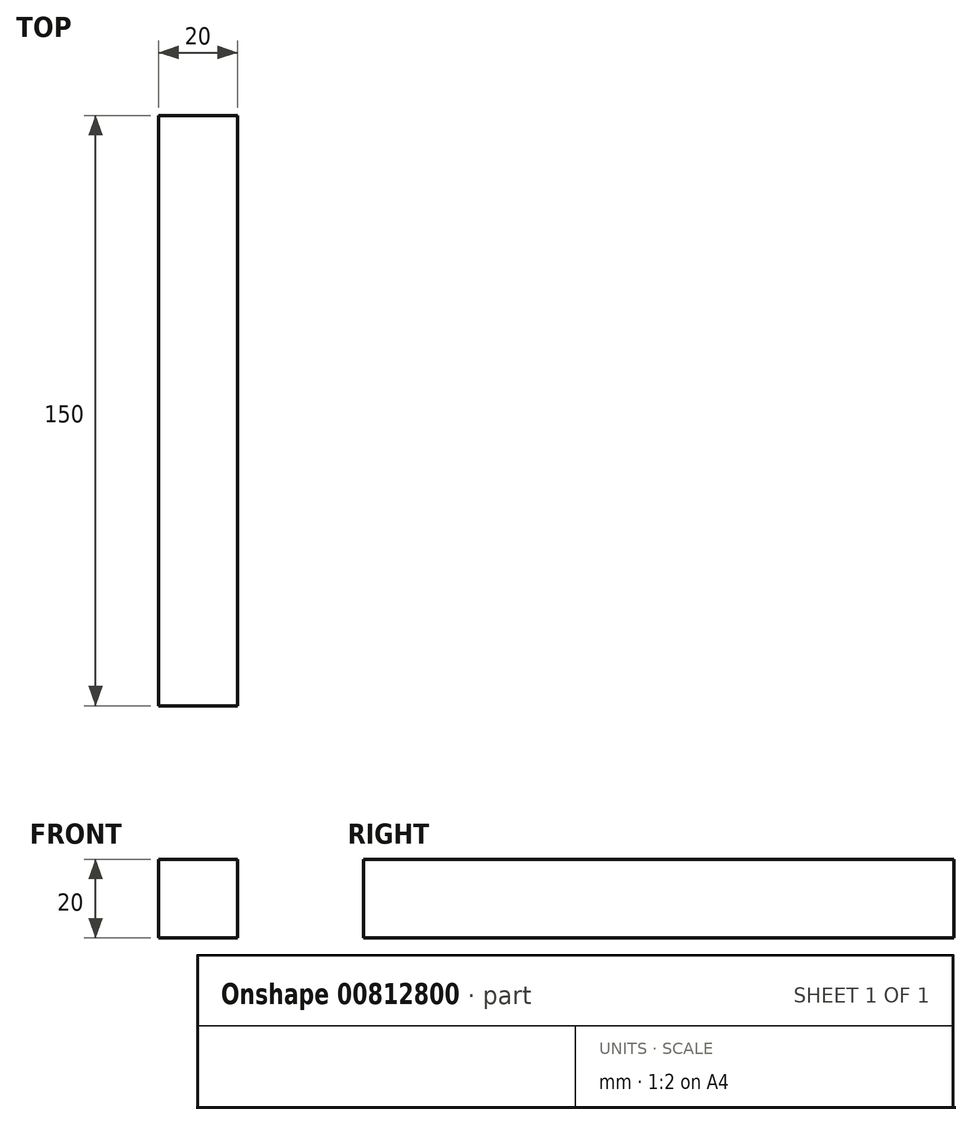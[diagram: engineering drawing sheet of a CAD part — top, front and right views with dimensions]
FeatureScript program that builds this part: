
annotation { "Feature Type Name" : "Feature", "Feature Type Description" : "" }
export const myFeature = defineFeature(function(context is Context, id is Id, definition is map)
    precondition{}
    {
        {
            var Q0;
            Q0=qCreatedBy(makeId("Front.planeOp"),FACE);
            var sketch = newSketch(context, id + "F0", { "sketchPlane" : qUnion([Q0])});
            skLineSegment(sketch, "E0.bottom", {"start": v(40.03, -35.4) * mm, "end": v(60.03, -35.4) * mm});
            skLineSegment(sketch, "E0.top", {"start": v(40.03, -55.4) * mm, "end": v(60.03, -55.4) * mm});
            skLineSegment(sketch, "E0.left", {"start": v(40.03, -35.4) * mm, "end": v(40.03, -55.4) * mm});
            skLineSegment(sketch, "E0.right", {"start": v(60.03, -35.4) * mm, "end": v(60.03, -55.4) * mm});
            skSolve(sketch);
        }
        {
            var Q0;
            Q0=makeQuery(id+"F0.imprint","IMPRINT",FACE,{"disambiguationData":[TD([[makeQuery(id+"F0.imprint","IMPRINT",EDGE,{"derivedFrom":sQuery(id+"F0.wireOp",EDGE,"E0.bottom")}),-1.0]])]});
            extrude(context, id + "F1", {"entities" : qUnion([Q0]), "depth" : 150 * mm, "offsetDistance" : 25 * mm});
        }
    });
